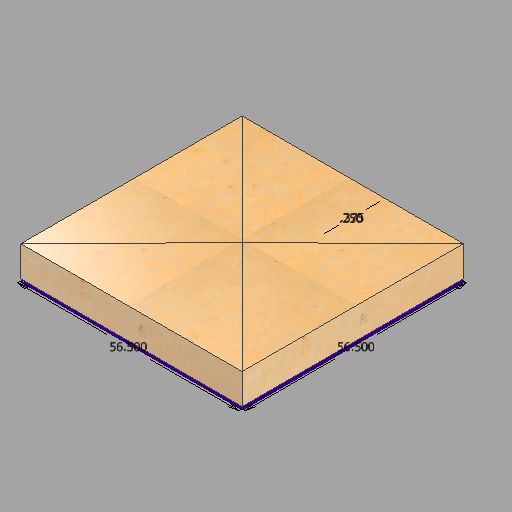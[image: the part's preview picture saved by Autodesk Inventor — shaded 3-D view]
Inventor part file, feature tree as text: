
AUTODESK INVENTOR PART (.ipt)
format: ipt  version: 2022.2 (Build 262287010, 287A)  size: 289,792 bytes
history: native  units: in
note: dims shown in document units (in); Inventor stores cm internally (conversion verified against a paired STEP export)
features: extrude x5, sketch x3, projected_geometry x2
ambient origin geometry x8: Origin, YZ Plane, XZ Plane, XY Plane, X Axis, Y Axis, Z Axis, Center Point
bodies: Solid1 (feature_tree)
feature tree (10):
  sketch  "Sketch1"  dims[d0=56.5in d1=56.5in]
  extrude  "Extrusion1"  Depth=56.5in
  sketch  "Sketch2"  dims[d2=0.375in d3=0.25in]
  sketch  "Sketch3"  dims[d4=8.5in d5=0.0in d6=0.25in d7=0.25in d8=0.25in d9=0.25in d10=0.0in d11=0.0in d12=0.0in d13=0.0in d14=0.75in d15=0.0in d16=0.5in d17=0.0in]
  extrude  "Extrusion2"  Depth=0.25in
  extrude  "Extrusion3"  Depth=0.25in
  extrude  "Extrusion4"  Depth=0.25in
  extrude  "Extrusion5"  Depth=0.25in
  projected_geometry  "Projected Loop1"
  projected_geometry  "Projected Loop2"
